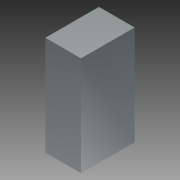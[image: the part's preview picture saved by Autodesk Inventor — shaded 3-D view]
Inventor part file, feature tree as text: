
AUTODESK INVENTOR PART (.ipt)
format: ipt  version: 2015 (Build 190159000, 159)  size: 92,672 bytes
history: native  units: in
note: dims shown in document units (in); Inventor stores cm internally (conversion verified against a paired STEP export)
features: extrude x1, sketch x1
ambient origin geometry x8: Origin, YZ Plane, XZ Plane, XY Plane, X Axis, Y Axis, Z Axis, Center Point
bodies: Solid1 (feature_tree)
feature tree (2):
  extrude  "Extrusion1"  Depth=42.0in
  sketch  "Sketch1"  dims[d0=28.0in d1=42.0in d2=78.0in d3=0.0in]
